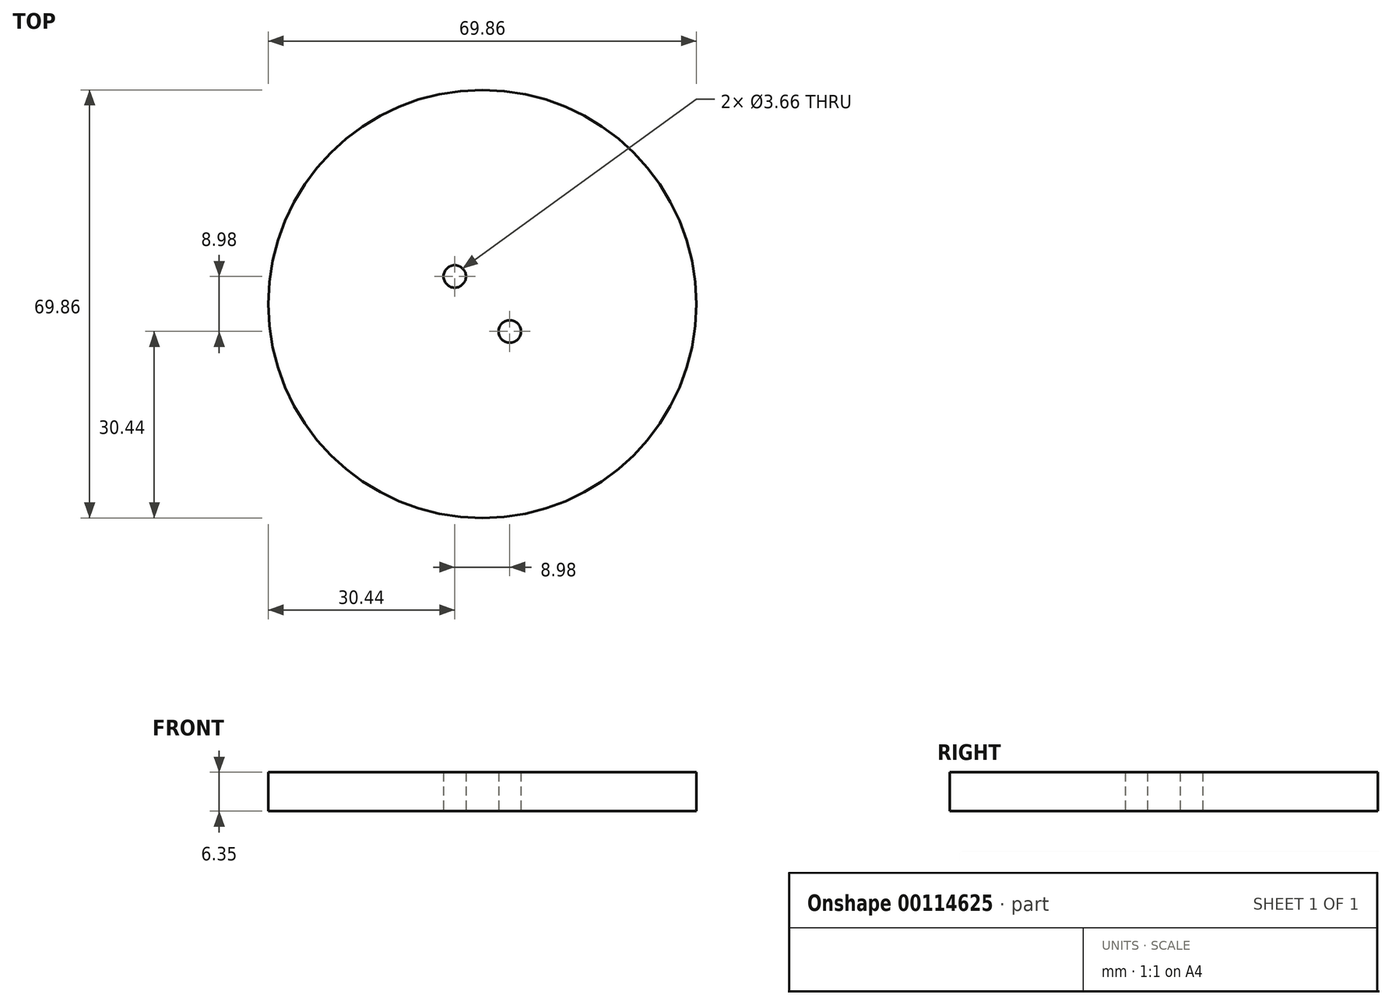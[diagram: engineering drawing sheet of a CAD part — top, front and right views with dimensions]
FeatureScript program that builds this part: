
annotation { "Feature Type Name" : "Feature", "Feature Type Description" : "" }
export const myFeature = defineFeature(function(context is Context, id is Id, definition is map)
    precondition{}
    {
        {
            var Q0;
            Q0=qCreatedBy(makeId("Top.planeOp"),FACE);
            var sketch = newSketch(context, id + "F0", { "sketchPlane" : qUnion([Q0])});
            skCircle(sketch, "E0", {"center": v(0, 0) * mm, "radius": 34.93 * mm});
            skLineSegment(sketch, "E1", {"start": v(0, 0) * mm, "end": v(19.05, 0) * mm, "construction": true});
            skLineSegment(sketch, "E2", {"start": v(0, 0) * mm, "end": v(4.5, -4.5) * mm, "construction": true});
            skCircle(sketch, "E3", {"center": v(4.5, -4.5) * mm, "radius": 1.83 * mm});
            skLineSegment(sketch, "E4", {"start": v(0, 0) * mm, "end": v(8.62, 8.62) * mm, "construction": true});
            skCircle(sketch, "E5.MirrorC", {"center": v(-4.5, 4.5) * mm, "radius": 1.83 * mm});
            skSolve(sketch);
        }
        {
            var Q0;
            Q0 = qSketchRegion(id + "F0", true);
            extrude(context, id + "F1", {"entities" : qUnion([Q0]), "depth" : 6.35 * mm});
        }
    });
